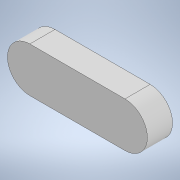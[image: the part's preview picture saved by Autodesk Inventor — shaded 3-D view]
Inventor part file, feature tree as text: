
AUTODESK INVENTOR PART (.ipt)
format: ipt  version: 2020 (Build 240168000, 168)  size: 96,768 bytes
history: native  units: mm
features: extrude x1, sketch x1
ambient origin geometry x8: Origin, YZ Plane, XZ Plane, XY Plane, X Axis, Y Axis, Z Axis, Center Point
bodies: Body1 (feature_tree)
feature tree (2):
  extrude  "拉伸2"  Depth=32.0mm
  sketch  "草图1"  dims[d2=100.0mm d3=32.0mm d4=18.0mm d5=0.0mm]
